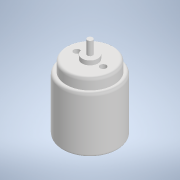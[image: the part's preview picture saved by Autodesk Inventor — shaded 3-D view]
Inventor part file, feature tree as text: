
AUTODESK INVENTOR PART (.ipt)
format: ipt  version: 2022 (Build 260153070, 153G)  size: 176,640 bytes
history: native  units: in
note: dims shown in document units (in); Inventor stores cm internally (conversion verified against a paired STEP export)
features: sketch x3, extrude x2, revolve x1, fillet x1
ambient origin geometry x8: Origin, YZ Plane, XZ Plane, XY Plane, X Axis, Y Axis, Z Axis, Center Point
bodies: Body1 (feature_tree)
feature tree (7):
  revolve  "Revolution1"  [1 undecoded]
  fillet  "Fillet1"  Radius=0.0394in
  extrude  "Extrusion2"  TaperAngle=90.0deg  [1 undecoded]
  extrude  "Extrusion3"  Depth=0.1181in
  sketch  "Sketch3"  dims[d5=0.1673in d7=0.063in d10=0.0394in]
  sketch  "Sketch4"  dims[d13=0.0787in d14=90.0deg]
  sketch  "Sketch5"  dims[d15=0.0394in d16=0.1181in d17=0.315in d18=0.9843in d19=0.0591in d20=0.1575in d21=0.4134in d23=0.2461in d24=0.3937in d25=0.0906in d26=0.7874in d28=360.0deg d30=0.0787in d31=0.0in d32=0.1181in d33=0.0in]
note: 2 required parameter values undecoded (feature->parameter linkage not recoverable at this tier; creation-order binding heuristic only, values carry confidence <= 0.55)